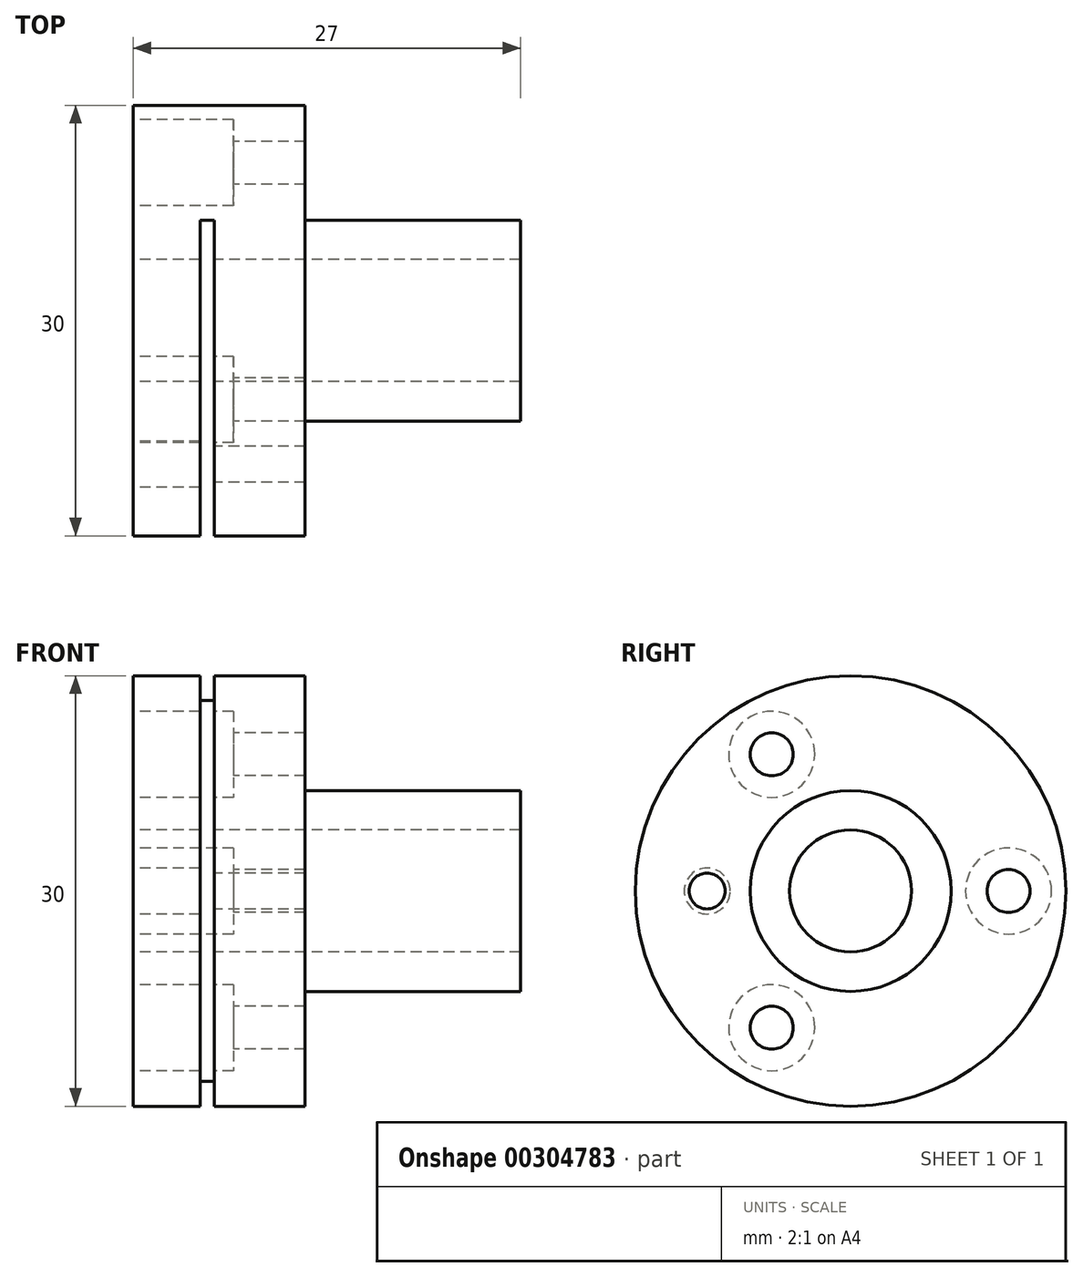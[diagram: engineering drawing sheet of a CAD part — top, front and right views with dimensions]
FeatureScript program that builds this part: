
annotation { "Feature Type Name" : "Feature", "Feature Type Description" : "" }
export const myFeature = defineFeature(function(context is Context, id is Id, definition is map)
    precondition{}
    {
        {
            var Q0;
            Q0=qCreatedBy(makeId("Top.planeOp"),FACE);
            var sketch = newSketch(context, id + "F0", { "sketchPlane" : qUnion([Q0])});
            skLineSegment(sketch, "E0", {"start": v(0, 4.25) * mm, "end": v(0, 15) * mm});
            skLineSegment(sketch, "E1", {"start": v(0, 15) * mm, "end": v(12, 15) * mm});
            skLineSegment(sketch, "E2", {"start": v(12, 15) * mm, "end": v(12, 7) * mm});
            skLineSegment(sketch, "E3", {"start": v(12, 7) * mm, "end": v(27, 7) * mm});
            skLineSegment(sketch, "E4", {"start": v(27, 4.25) * mm, "end": v(0, 4.25) * mm});
            skLineSegment(sketch, "E5", {"start": v(27, 7) * mm, "end": v(27, 4.25) * mm});
            skLineSegment(sketch, "E6", {"start": v(-52.03, 0) * mm, "end": v(151.17, 0) * mm, "construction": true});
            skSolve(sketch);
        }
        {
            var Q0;
            Q0=makeQuery(id+"F0.imprint","IMPRINT",FACE,{"disambiguationData":[TD([[makeQuery(id+"F0.imprint","IMPRINT",EDGE,{"derivedFrom":sQuery(id+"F0.wireOp",EDGE,"E0")}),-1.0]])]});
            var Q1;
            Q1=sQuery(id+"F0.wireOp",EDGE,"E6");
            revolve(context, id + "F1", {"surfaceOperationType" : NewSurfaceOperationType.NEW, "entities" : qUnion([Q0]), "axis" : qUnion([Q1]), "revolveType" : RevolveType.FULL});
        }
        {
            var Q0;
            Q0=makeQuery(id+"F1.opRevolve","SWEPT_FACE",FACE,{"disambiguationData":[OSD([sQuery(id+"F0.wireOp",EDGE,"E0")])]});
            var sketch = newSketch(context, id + "F2", { "sketchPlane" : qUnion([Q0])});
            skCircle(sketch, "E7", {"center": v(5.5, 9.53) * mm, "radius": 1.5 * mm});
            skCircle(sketch, "E8", {"center": v(-11, 0) * mm, "radius": 1.5 * mm});
            skCircle(sketch, "E9", {"center": v(0, 0) * mm, "radius": 11 * mm, "construction": true});
            skCircle(sketch, "E10", {"center": v(5.5, -9.53) * mm, "radius": 1.5 * mm});
            skLineSegment(sketch, "E11", {"start": v(-11, 0) * mm, "end": v(5.5, -9.53) * mm, "construction": true});
            skLineSegment(sketch, "E12", {"start": v(-11, 0) * mm, "end": v(5.5, 9.53) * mm, "construction": true});
            skLineSegment(sketch, "E13", {"start": v(5.5, 9.53) * mm, "end": v(5.5, -9.53) * mm, "construction": true});
            skSolve(sketch);
        }
        {
            var Q0;
            Q0=makeQuery(id+"F2.imprint","IMPRINT",FACE,{"disambiguationData":[TD([[makeQuery(id+"F2.imprint","IMPRINT",EDGE,{"derivedFrom":sQuery(id+"F2.wireOp",EDGE,"E7")}),1.0]])]});
            var Q1;
            Q1=makeQuery(id+"F2.imprint","IMPRINT",FACE,{"disambiguationData":[TD([[makeQuery(id+"F2.imprint","IMPRINT",EDGE,{"derivedFrom":sQuery(id+"F2.wireOp",EDGE,"E8")}),1.0]])]});
            var Q2;
            Q2=makeQuery(id+"F2.imprint","IMPRINT",FACE,{"disambiguationData":[TD([[makeQuery(id+"F2.imprint","IMPRINT",EDGE,{"derivedFrom":sQuery(id+"F2.wireOp",EDGE,"E10")}),1.0]])]});
            extrude(context, id + "F3", {"entities" : qUnion([Q0, Q1, Q2]), "operationType" : NewBodyOperationType.REMOVE, "endBound" : BoundingType.THROUGH_ALL, "oppositeDirection" : true, "depth" : 7 * mm, "offsetDistance" : 25 * mm});
        }
        {
            var Q0;
            Q0=makeQuery(id+"F1.opRevolve","SWEPT_FACE",FACE,{"disambiguationData":[OSD([sQuery(id+"F0.wireOp",EDGE,"E0")])]});
            var sketch = newSketch(context, id + "F4", { "sketchPlane" : qUnion([Q0])});
            skCircle(sketch, "E14", {"center": v(5.5, 9.53) * mm, "radius": 3 * mm});
            skCircle(sketch, "E15", {"center": v(-11, 0) * mm, "radius": 3 * mm});
            skCircle(sketch, "E16", {"center": v(5.5, -9.53) * mm, "radius": 3 * mm});
            skSolve(sketch);
        }
        {
            var Q0;
            Q0=makeQuery(id+"F4.imprint","IMPRINT",FACE,{"disambiguationData":[TD([[makeQuery(id+"F4.imprint","IMPRINT",EDGE,{"derivedFrom":sQuery(id+"F4.wireOp",EDGE,"E14")}),1.0]])]});
            var Q1;
            Q1=makeQuery(id+"F4.imprint","IMPRINT",FACE,{"disambiguationData":[TD([[makeQuery(id+"F4.imprint","IMPRINT",EDGE,{"derivedFrom":sQuery(id+"F4.wireOp",EDGE,"E15")}),1.0]])]});
            var Q2;
            Q2=makeQuery(id+"F4.imprint","IMPRINT",FACE,{"disambiguationData":[TD([[makeQuery(id+"F4.imprint","IMPRINT",EDGE,{"derivedFrom":sQuery(id+"F4.wireOp",EDGE,"E16")}),1.0]])]});
            extrude(context, id + "F5", {"entities" : qUnion([Q0, Q1, Q2]), "operationType" : NewBodyOperationType.REMOVE, "oppositeDirection" : true, "depth" : 7 * mm, "offsetDistance" : 25 * mm});
        }
        {
            var Q0;
            Q0=qCreatedBy(makeId("Front.planeOp"),FACE);
            var sketch = newSketch(context, id + "F6", { "sketchPlane" : qUnion([Q0])});
            skLineSegment(sketch, "E17.bottom", {"start": v(4.68, 22.5) * mm, "end": v(5.68, 22.5) * mm});
            skLineSegment(sketch, "E17.top", {"start": v(4.68, -22.5) * mm, "end": v(5.68, -22.5) * mm});
            skLineSegment(sketch, "E17.left", {"start": v(4.68, 22.5) * mm, "end": v(4.68, -22.5) * mm});
            skLineSegment(sketch, "E17.right", {"start": v(5.68, 22.5) * mm, "end": v(5.68, -22.5) * mm});
            skPoint(sketch, "E18", {"position": v(4.68, 0) * mm});
            skSolve(sketch);
        }
        {
            var Q0;
            Q0=makeQuery(id+"F6.imprint","IMPRINT",FACE,{"disambiguationData":[TD([[makeQuery(id+"F6.imprint","IMPRINT",EDGE,{"derivedFrom":sQuery(id+"F6.wireOp",EDGE,"E17.bottom")}),-1.0]])]});
            extrude(context, id + "F7", {"entities" : qUnion([Q0]), "operationType" : NewBodyOperationType.REMOVE, "oppositeDirection" : true, "depth" : 7 * mm, "offsetDistance" : 25 * mm, "hasSecondDirection" : true, "secondDirectionOppositeDirection" : false, "secondDirectionDepth" : 25 * mm});
        }
        {
            var Q0;
            Q0=makeQuery(id+"F1.opRevolve","SWEPT_FACE",FACE,{"disambiguationData":[OSD([sQuery(id+"F0.wireOp",EDGE,"E0")])]});
            var sketch = newSketch(context, id + "F8", { "sketchPlane" : qUnion([Q0])});
            skCircle(sketch, "E19", {"center": v(10, 0) * mm, "radius": 1.25 * mm});
            skSolve(sketch);
        }
        {
            var Q0;
            Q0=makeQuery(id+"F8.imprint","IMPRINT",FACE,{"disambiguationData":[TD([[makeQuery(id+"F8.imprint","IMPRINT",EDGE,{"derivedFrom":sQuery(id+"F8.wireOp",EDGE,"E19")}),1.0]])]});
            extrude(context, id + "F9", {"entities" : qUnion([Q0]), "operationType" : NewBodyOperationType.REMOVE, "endBound" : BoundingType.THROUGH_ALL, "oppositeDirection" : true, "depth" : 25 * mm, "offsetDistance" : 25 * mm});
        }
        {
            var Q0;
            Q0=makeQuery(id+"F1.opRevolve","SWEPT_FACE",FACE,{"disambiguationData":[OSD([sQuery(id+"F0.wireOp",EDGE,"E0")])]});
            var sketch = newSketch(context, id + "F10", { "sketchPlane" : qUnion([Q0])});
            skCircle(sketch, "E20", {"center": v(10, 0) * mm, "radius": 1.6 * mm});
            skSolve(sketch);
        }
        {
            var Q0;
            Q0=makeQuery(id+"F10.imprint","IMPRINT",FACE,{"disambiguationData":[TD([[makeQuery(id+"F10.imprint","IMPRINT",EDGE,{"derivedFrom":sQuery(id+"F10.wireOp",EDGE,"E20")}),1.0]])]});
            extrude(context, id + "F11", {"entities" : qUnion([Q0]), "operationType" : NewBodyOperationType.REMOVE, "oppositeDirection" : true, "depth" : 5 * mm, "offsetDistance" : 25 * mm});
        }
    });
